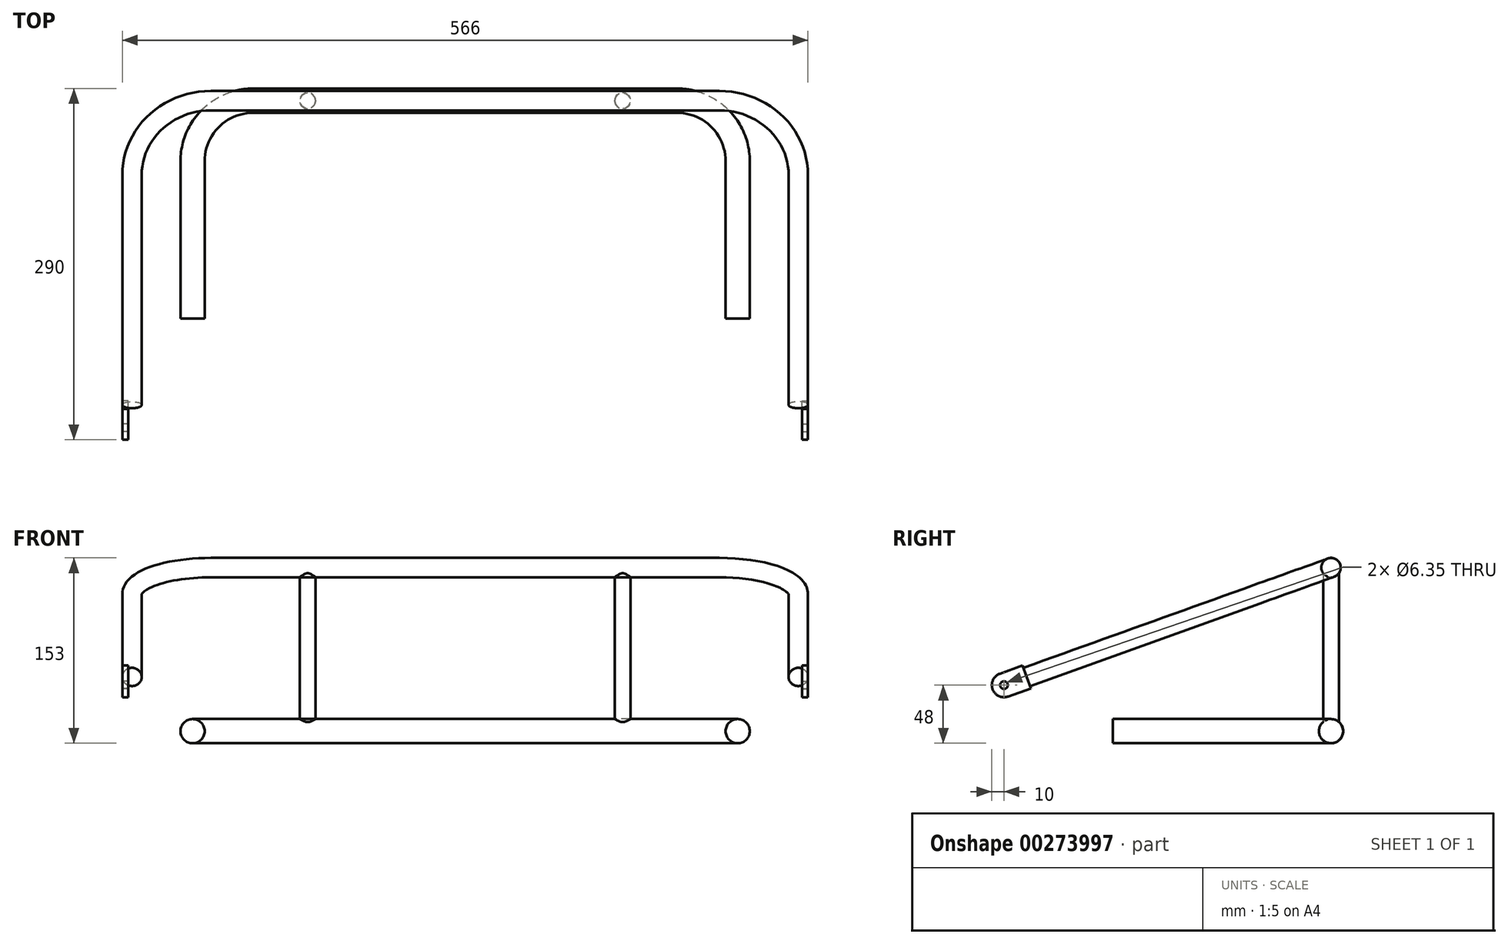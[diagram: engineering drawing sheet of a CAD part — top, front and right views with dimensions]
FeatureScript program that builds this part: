
annotation { "Feature Type Name" : "Feature", "Feature Type Description" : "" }
export const myFeature = defineFeature(function(context is Context, id is Id, definition is map)
    precondition{}
    {
        {
            var Q0;
            Q0=qCreatedBy(makeId("Top.planeOp"),FACE);
            var sketch = newSketch(context, id + "F0", { "sketchPlane" : qUnion([Q0])});
            skLineSegment(sketch, "E0", {"start": v(-225, -150) * mm, "end": v(-225, -50) * mm});
            skLineSegment(sketch, "E1", {"start": v(-175, 0) * mm, "end": v(175, 0) * mm});
            skLineSegment(sketch, "E2", {"start": v(225, -50) * mm, "end": v(225, -150) * mm});
            skPoint(sketch, "E3.visualSharp", {"position": v(-225, 0) * mm});
            skArc(sketch, "E3.filletArc", {"start": v(-175, 0) * mm, "mid": v(-210.36, -14.64) * mm, "end": v(-225, -50) * mm});
            skPoint(sketch, "E4.visualSharp", {"position": v(225, 0) * mm});
            skArc(sketch, "E4.filletArc", {"start": v(225, -50) * mm, "mid": v(210.36, -14.64) * mm, "end": v(175, 0) * mm});
            skSolve(sketch);
        }
        {
            var Q0;
            Q0=sQuery(id+"F0.wireOp",VERTEX,"E2.end");
            var Q1;
            Q1=sQuery(id+"F0.wireOp",EDGE,"E2");
            cPlane(context, id + "F1", {"entities" : qUnion([Q0, Q1]), "cplaneType" : CPlaneType.LINE_POINT, "offset" : 150 * mm, "width" : 150 * mm, "height" : 150 * mm});
        }
        {
            var Q0;
            Q0=qCreatedBy(id+"F1.planeOp",FACE);
            var sketch = newSketch(context, id + "F2", { "sketchPlane" : qUnion([Q0])});
            skPoint(sketch, "E5.0", {"position": v(225, 0) * mm});
            skCircle(sketch, "E6", {"center": v(225, 0) * mm, "radius": 10 * mm});
            skSolve(sketch);
        }
        {
            var Q0;
            Q0=makeQuery(id+"F2.imprint","IMPRINT",FACE,{"disambiguationData":[TD([[makeQuery(id+"F2.imprint","IMPRINT",EDGE,{"derivedFrom":sQuery(id+"F2.wireOp",EDGE,"E6")}),1.0]])]});
            var Q1;
            Q1=sQuery(id+"F0.wireOp",EDGE,"E2");
            var Q2;
            Q2=sQuery(id+"F0.wireOp",EDGE,"E4.filletArc");
            var Q3;
            Q3=sQuery(id+"F0.wireOp",EDGE,"E1");
            var Q4;
            Q4=sQuery(id+"F0.wireOp",EDGE,"E3.filletArc");
            var Q5;
            Q5=sQuery(id+"F0.wireOp",EDGE,"E0");
            sweep(context, id + "F3", {"profiles" : qUnion([Q0]), "path" : qUnion([Q1, Q2, Q3, Q4, Q5])});
        }
        {
            var Q0;
            Q0=qCreatedBy(makeId("Front.planeOp"),FACE);
            var sketch = newSketch(context, id + "F4", { "sketchPlane" : qUnion([Q0])});
            skLineSegment(sketch, "E7", {"start": v(210, 135) * mm, "end": v(-210, 135) * mm});
            skPoint(sketch, "E8", {"position": v(0, 135) * mm});
            skSolve(sketch);
        }
        {
            var Q0;
            Q0=makeQuery(id+"F3.opSweep","CAP_FACE",FACE,{"disambiguationData":[OSD([sQuery(id+"F0.wireOp",VERTEX,"E2.end"),sQuery(id+"F2.wireOp",EDGE,"E6")])],"isStart":true});
            cPlane(context, id + "F5", {"entities" : qUnion([Q0]), "cplaneType" : CPlaneType.OFFSET, "offset" : 120 * mm, "width" : 150 * mm, "height" : 150 * mm});
        }
        {
            var Q0;
            Q0=qCreatedBy(id+"F5.planeOp",FACE);
            var sketch = newSketch(context, id + "F6", { "sketchPlane" : qUnion([Q0])});
            skPoint(sketch, "E9.0", {"position": v(225, 0) * mm});
            skLineSegment(sketch, "E10.bottom", {"start": v(225, 0) * mm, "end": v(275, 0) * mm});
            skLineSegment(sketch, "E10.top", {"start": v(225, 38) * mm, "end": v(275, 38) * mm});
            skLineSegment(sketch, "E10.left", {"start": v(225, 0) * mm, "end": v(225, 38) * mm});
            skLineSegment(sketch, "E10.right", {"start": v(275, 0) * mm, "end": v(275, 38) * mm});
            skSolve(sketch);
        }
        {
            var Q0;
            Q0=sQuery(id+"F4.wireOp",VERTEX,"E7.end");
            var Q1;
            Q1=sQuery(id+"F4.wireOp",VERTEX,"E7.start");
            var Q2;
            Q2=sQuery(id+"F6.wireOp",VERTEX,"E10.top.end");
            cPlane(context, id + "F7", {"entities" : qUnion([Q0, Q1, Q2]), "cplaneType" : CPlaneType.THREE_POINT, "offset" : 150 * mm, "width" : 150 * mm, "height" : 150 * mm});
        }
        {
            var Q0;
            Q0=qCreatedBy(id+"F7.planeOp",FACE);
            var sketch = newSketch(context, id + "F8", { "sketchPlane" : qUnion([Q0])});
            skLineSegment(sketch, "E11.0", {"start": v(210, 45.64) * mm, "end": v(-210, 45.64) * mm});
            skPoint(sketch, "E12.0", {"position": v(275, -241.25) * mm});
            skLineSegment(sketch, "E13", {"start": v(275, -221.25) * mm, "end": v(275, -19.36) * mm});
            skArc(sketch, "E14", {"start": v(275, -19.36) * mm, "mid": v(255.96, 26.6) * mm, "end": v(210, 45.64) * mm});
            skPoint(sketch, "E15", {"position": v(275, -221.25) * mm});
            skLineSegment(sketch, "E16", {"start": v(0, 45.64) * mm, "end": v(0, -160.44) * mm, "construction": true});
            skPoint(sketch, "E16.endSnap0", {"position": v(0, 45.64) * mm});
            skLineSegment(sketch, "E17.MirrorCS", {"start": v(-275, -221.25) * mm, "end": v(-275, -19.36) * mm});
            skArc(sketch, "E18.MirrorCS", {"start": v(-275, -19.36) * mm, "mid": v(-255.96, 26.6) * mm, "end": v(-210, 45.64) * mm});
            skSolve(sketch);
        }
        {
            var Q0;
            Q0=sQuery(id+"F8.wireOp",VERTEX,"E15");
            var Q1;
            Q1=sQuery(id+"F8.wireOp",EDGE,"E13");
            cPlane(context, id + "F9", {"entities" : qUnion([Q0, Q1]), "cplaneType" : CPlaneType.LINE_POINT, "offset" : 150 * mm, "width" : 150 * mm, "height" : 150 * mm});
        }
        {
            var Q0;
            Q0=qCreatedBy(id+"F9.planeOp",FACE);
            var sketch = newSketch(context, id + "F10", { "sketchPlane" : qUnion([Q0])});
            skPoint(sketch, "E19.0", {"position": v(-275, 127.05) * mm});
            skCircle(sketch, "E20", {"center": v(-275, 127.05) * mm, "radius": 8 * mm});
            skSolve(sketch);
        }
        {
            var Q0;
            Q0=makeQuery(id+"F10.imprint","IMPRINT",FACE,{"disambiguationData":[TD([[makeQuery(id+"F10.imprint","IMPRINT",EDGE,{"derivedFrom":sQuery(id+"F10.wireOp",EDGE,"E20")}),1.0]])]});
            var Q1;
            Q1=sQuery(id+"F8.wireOp",EDGE,"E13");
            var Q2;
            Q2=sQuery(id+"F8.wireOp",EDGE,"E14");
            var Q3;
            Q3=sQuery(id+"F8.wireOp",EDGE,"E11.0");
            var Q4;
            Q4=sQuery(id+"F8.wireOp",EDGE,"E18.MirrorCS");
            var Q5;
            Q5=sQuery(id+"F8.wireOp",EDGE,"E17.MirrorCS");
            sweep(context, id + "F11", {"profiles" : qUnion([Q0]), "path" : qUnion([Q1, Q2, Q3, Q4, Q5])});
        }
        {
            var Q0;
            Q0=qCreatedBy(makeId("Top.planeOp"),FACE);
            cPlane(context, id + "F12", {"entities" : qUnion([Q0]), "cplaneType" : CPlaneType.OFFSET, "offset" : 50 * mm, "width" : 150 * mm, "height" : 150 * mm});
        }
        {
            var Q0;
            Q0=qCreatedBy(id+"F12.planeOp",FACE);
            var sketch = newSketch(context, id + "F13", { "sketchPlane" : qUnion([Q0])});
            skCircle(sketch, "E21", {"center": v(0, 0) * mm, "radius": 6.5 * mm});
            skSolve(sketch);
        }
        {
            var Q0;
            Q0=qSketchRegion(id+"F13",true);
            var Q1;
            Q1=makeQuery(id+"F11.opSweep","SWEPT_FACE",FACE,{"disambiguationData":[OSD([sQuery(id+"F8.wireOp",EDGE,"E11.0"),sQuery(id+"F10.wireOp",EDGE,"E20")])]});
            var Q2;
            Q2=makeQuery(id+"F3.opSweep","SWEPT_FACE",FACE,{"disambiguationData":[OSD([sQuery(id+"F0.wireOp",EDGE,"E1"),sQuery(id+"F2.wireOp",EDGE,"E6")])]});
            extrude(context, id + "F14", {"entities" : qUnion([Q0]), "endBound" : BoundingType.UP_TO_SURFACE, "endBoundEntityFace" : qUnion([Q1]), "depth" : 25 * mm, "hasSecondDirection" : true, "secondDirectionBound" : SecondDirectionBoundingType.UP_TO_SURFACE, "secondDirectionOppositeDirection" : true, "secondDirectionBoundEntityFace" : qUnion([Q2]), "secondDirectionDepth" : 25 * mm});
        }
        {
            var Q0;
            Q0=makeQuery(id+"F14.opExtrude","SWEPT_BODY",BODY,{"disambiguationData":[OSD([sQuery(id+"F13.wireOp",EDGE,"E21")])]});
            transform(context, id + "F15", {"entities" : qUnion([Q0]), "transformType" : TransformType.TRANSLATION_3D, "dx" : 130 * mm, "dy" : 0 * mm, "dz" : 0 * mm, "makeCopy" : false});
        }
        {
            var Q0;
            Q0=makeQuery(id+"F11.opSweep","CAP_FACE",FACE,{"disambiguationData":[OSD([sQuery(id+"F8.wireOp",VERTEX,"E13.start"),sQuery(id+"F10.wireOp",EDGE,"E20")])],"isStart":true});
            var sketch = newSketch(context, id + "F16", { "sketchPlane" : qUnion([Q0])});
            skPoint(sketch, "E22", {"position": v(275, 127.05) * mm});
            skLineSegment(sketch, "E23.bottom", {"start": v(278, 137.05) * mm, "end": v(282.8, 137.05) * mm});
            skLineSegment(sketch, "E23.top", {"start": v(278, 117.05) * mm, "end": v(282.8, 117.05) * mm});
            skLineSegment(sketch, "E23.left", {"start": v(278, 137.05) * mm, "end": v(278, 117.05) * mm});
            skLineSegment(sketch, "E23.right", {"start": v(282.8, 137.05) * mm, "end": v(282.8, 117.05) * mm});
            skLineSegment(sketch, "E24", {"start": v(275, 127.05) * mm, "end": v(278, 127.05) * mm, "construction": true});
            skSolve(sketch);
        }
        {
            var Q0;
            Q0=qSketchRegion(id+"F16",true);
            extrude(context, id + "F17", {"entities" : qUnion([Q0]), "depth" : 30 * mm});
        }
        {
            var Q0;
            Q0=makeQuery(id+"F17.opExtrude","SWEPT_FACE",FACE,{"disambiguationData":[OSD([sQuery(id+"F16.wireOp",EDGE,"E23.right")])]});
            var sketch = newSketch(context, id + "F18", { "sketchPlane" : qUnion([Q0])});
            skLineSegment(sketch, "E25.0", {"start": v(-282.8, 44.03) * mm, "end": v(-276.03, 25.2) * mm, "construction": true});
            skLineSegment(sketch, "E25.1", {"start": v(-282.8, 44.03) * mm, "end": v(-254.56, 54.17) * mm, "construction": true});
            skLineSegment(sketch, "E26", {"start": v(-279.41, 34.62) * mm, "end": v(-270, 38) * mm, "construction": true});
            skLineSegment(sketch, "E27", {"start": v(-270, 38) * mm, "end": v(-273.38, 47.41) * mm, "construction": true});
            skCircle(sketch, "E28", {"center": v(-270, 38) * mm, "radius": 3.17 * mm});
            skSolve(sketch);
        }
        {
            var Q0;
            Q0=qSketchRegion(id+"F18",true);
            extrude(context, id + "F19", {"entities" : qUnion([Q0]), "operationType" : NewBodyOperationType.REMOVE, "endBound" : BoundingType.THROUGH_ALL, "oppositeDirection" : true, "depth" : 25 * mm});
        }
        {
            var Q0;
            Q0=makeQuery(id+"F17.opExtrude","CAP_EDGE",EDGE,{"disambiguationData":[OSD([sQuery(id+"F16.wireOp",EDGE,"E23.bottom")])],"isStart":false});
            var Q1;
            Q1=makeQuery(id+"F17.opExtrude","CAP_EDGE",EDGE,{"disambiguationData":[OSD([sQuery(id+"F16.wireOp",EDGE,"E23.top")])],"isStart":false});
            fillet(context, id + "F20", {"entities" : qUnion([Q0, Q1]), "radius" : 10 * mm, "tangentPropagation" : true, "allowEdgeOverflow" : false});
        }
        {
            var Q0;
            Q0=makeQuery(id+"F17.opExtrude","SWEPT_BODY",BODY,{"disambiguationData":[OSD([sQuery(id+"F16.wireOp",EDGE,"E23.bottom"),sQuery(id+"F16.wireOp",EDGE,"E23.top"),sQuery(id+"F16.wireOp",EDGE,"E23.left"),sQuery(id+"F16.wireOp",EDGE,"E23.right")])]});
            var Q1;
            Q1=makeQuery(id+"F14.opExtrude","SWEPT_BODY",BODY,{"disambiguationData":[OSD([sQuery(id+"F13.wireOp",EDGE,"E21")])]});
            var Q2;
            Q2=qCreatedBy(makeId("Right.planeOp"),FACE);
            mirror(context, id + "F21", {"entities" : qUnion([Q0, Q1]), "mirrorPlane" : qUnion([Q2])});
        }
        {
            var Q0;
            Q0=makeQuery(id+"F3.opSweep","CAP_FACE",FACE,{"disambiguationData":[OSD([sQuery(id+"F0.wireOp",VERTEX,"E2.end"),sQuery(id+"F2.wireOp",EDGE,"E6")])],"isStart":true});
            var Q1;
            Q1=makeQuery(id+"F3.opSweep","CAP_FACE",FACE,{"disambiguationData":[OSD([sQuery(id+"F0.wireOp",VERTEX,"E0.start"),sQuery(id+"F2.wireOp",EDGE,"E6")])],"isStart":false});
            extrude(context, id + "F22", {"entities" : qUnion([Q0, Q1]), "operationType" : NewBodyOperationType.ADD, "depth" : 30 * mm});
        }
    });
